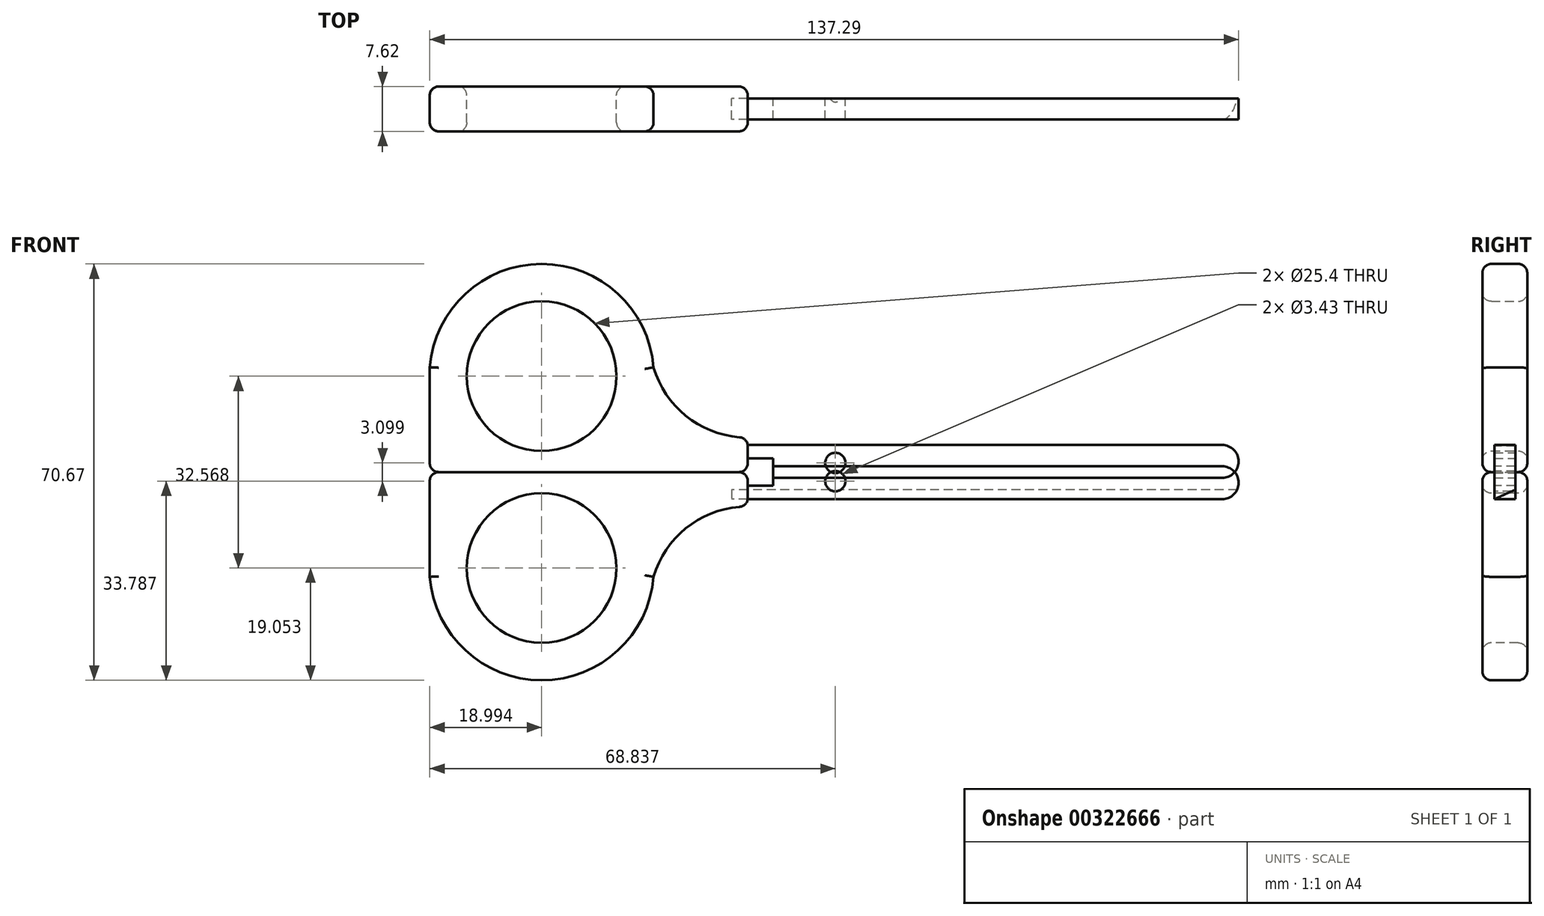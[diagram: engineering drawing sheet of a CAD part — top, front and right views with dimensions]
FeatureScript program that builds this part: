
annotation { "Feature Type Name" : "Feature", "Feature Type Description" : "" }
export const myFeature = defineFeature(function(context is Context, id is Id, definition is map)
    precondition{}
    {
        {
            var Q0;
            Q0=qCreatedBy(makeId("Front.planeOp"),FACE);
            var sketch = newSketch(context, id + "F0", { "sketchPlane" : qUnion([Q0])});
            skArc(sketch, "E0", {"start": v(-13.22, 18.69) * mm, "mid": v(-32.22, 36.24) * mm, "end": v(-51.2, 18.69) * mm});
            skLineSegment(sketch, "E1", {"start": v(-51.2, 18.69) * mm, "end": v(-51.2, 0.9) * mm});
            skLineSegment(sketch, "E2", {"start": v(-51.2, 0.9) * mm, "end": v(2.77, 0.9) * mm});
            skLineSegment(sketch, "E3", {"start": v(2.77, 0.9) * mm, "end": v(2.77, 6.77) * mm});
            skCircle(sketch, "E4", {"center": v(-32.22, 17.2) * mm, "radius": 12.7 * mm});
            skLineSegment(sketch, "E5", {"start": v(6.8, 7.3) * mm, "end": v(6.8, 7.3) * mm});
            skArc(sketch, "E6.filletArc", {"start": v(-13.22, 18.69) * mm, "mid": v(-5.52, 8.93) * mm, "end": v(6.8, 7.3) * mm});
            skSolve(sketch);
        }
        {
            var Q0;
            Q0=qSketchRegion(id+"F0",true);
            extrude(context, id + "F1", {"entities" : qUnion([Q0]), "endBound" : BoundingType.SYMMETRIC, "depth" : 7.62 * mm});
        }
        {
            var Q0;
            Q0=makeQuery(id+"F1.opExtrude","CAP_EDGE",EDGE,{"disambiguationData":[OSD([sQuery(id+"F0.wireOp",EDGE,"9kog8hWk-n0xC-SFov-Do0S-5giGeTCsTdrN")])],"isStart":false});
            var Q1;
            Q1=makeQuery(id+"F1.opExtrude","CAP_EDGE",EDGE,{"disambiguationData":[OSD([sQuery(id+"F0.wireOp",EDGE,"9kog8hWk-n0xC-SFov-Do0S-5giGeTCsTdrN")])],"isStart":true});
            var Q2;
            Q2=makeQuery(id+"F1.opExtrude","CAP_EDGE",EDGE,{"disambiguationData":[OSD([sQuery(id+"F0.wireOp",EDGE,"E3")])],"isStart":false});
            var Q3;
            Q3=makeQuery(id+"F1.opExtrude","CAP_EDGE",EDGE,{"disambiguationData":[OSD([sQuery(id+"F0.wireOp",EDGE,"E2")])],"isStart":false});
            var Q4;
            Q4=makeQuery(id+"F1.opExtrude","SWEPT_EDGE",EDGE,{"disambiguationData":[OSD([sQuery(id+"F0.wireOp",EDGE,"E2"),sQuery(id+"F0.wireOp",EDGE,"E3")])]});
            var Q5;
            Q5=makeQuery(id+"F1.opExtrude","CAP_EDGE",EDGE,{"disambiguationData":[OSD([sQuery(id+"F0.wireOp",EDGE,"E4")])],"isStart":false});
            var Q6;
            Q6=makeQuery(id+"F1.opExtrude","CAP_EDGE",EDGE,{"disambiguationData":[OSD([sQuery(id+"F0.wireOp",EDGE,"E4")])],"isStart":true});
            var Q7;
            Q7=makeQuery(id+"F1.opExtrude","CAP_EDGE",EDGE,{"disambiguationData":[OSD([sQuery(id+"F0.wireOp",EDGE,"E1")])],"isStart":true});
            var Q8;
            Q8=makeQuery(id+"F1.opExtrude","CAP_EDGE",EDGE,{"disambiguationData":[OSD([sQuery(id+"F0.wireOp",EDGE,"E1")])],"isStart":false});
            var Q9;
            Q9=makeQuery(id+"F1.opExtrude","SWEPT_EDGE",EDGE,{"disambiguationData":[OSD([sQuery(id+"F0.wireOp",EDGE,"E1"),sQuery(id+"F0.wireOp",EDGE,"E2")])]});
            var Q10;
            Q10=makeQuery(id+"F1.opExtrude","CAP_EDGE",EDGE,{"disambiguationData":[OSD([sQuery(id+"F0.wireOp",EDGE,"E6.filletArc")])],"isStart":true});
            var Q11;
            Q11=makeQuery(id+"F1.opExtrude","CAP_EDGE",EDGE,{"disambiguationData":[OSD([sQuery(id+"F0.wireOp",EDGE,"E2")])],"isStart":true});
            var Q12;
            Q12=makeQuery(id+"F1.opExtrude","CAP_EDGE",EDGE,{"disambiguationData":[OSD([sQuery(id+"F0.wireOp",EDGE,"E3")])],"isStart":true});
            var Q13;
            Q13=makeQuery(id+"F1.opExtrude","CAP_EDGE",EDGE,{"disambiguationData":[OSD([sQuery(id+"F0.wireOp",EDGE,"E6.filletArc")])],"isStart":false});
            var Q14;
            Q14=makeQuery(id+"F1.opExtrude","CAP_EDGE",EDGE,{"disambiguationData":[OSD([sQuery(id+"F0.wireOp",EDGE,"E0")])],"isStart":false});
            var Q15;
            Q15=makeQuery(id+"F1.opExtrude","CAP_EDGE",EDGE,{"disambiguationData":[OSD([sQuery(id+"F0.wireOp",EDGE,"E0")])],"isStart":true});
            var Q16;
            Q16=makeQuery(id+"F1.opExtrude","SWEPT_EDGE",EDGE,{"disambiguationData":[OSD([sQuery(id+"F0.wireOp",EDGE,"E3"),sQuery(id+"F0.wireOp",EDGE,"E6.filletArc")])]});
            fillet(context, id + "F2", {"entities" : qUnion([Q0, Q1, Q2, Q3, Q4, Q5, Q6, Q7, Q8, Q9, Q10, Q11, Q12, Q13, Q14, Q15, Q16]), "radius" : 1.52 * mm, "tangentPropagation" : true, "allowEdgeOverflow" : false});
        }
        {
            var Q0;
            Q0=qCreatedBy(makeId("Front.planeOp"),FACE);
            var sketch = newSketch(context, id + "F3", { "sketchPlane" : qUnion([Q0])});
            skLineSegment(sketch, "E7", {"start": v(2.77, 5.5) * mm, "end": v(83.29, 5.5) * mm});
            skArc(sketch, "E8", {"start": v(83.29, -0.08) * mm, "mid": v(86.08, 2.71) * mm, "end": v(83.29, 5.5) * mm});
            skLineSegment(sketch, "E9", {"start": v(83.29, -0.08) * mm, "end": v(7.09, -0.08) * mm});
            skLineSegment(sketch, "E10", {"start": v(7.09, -0.08) * mm, "end": v(7.09, 3.22) * mm});
            skLineSegment(sketch, "E11", {"start": v(7.09, 3.22) * mm, "end": v(2.77, 3.22) * mm});
            skCircle(sketch, "E12", {"center": v(17.63, 2.46) * mm, "radius": 1.71 * mm});
            skLineSegment(sketch, "E13", {"start": v(2.77, 5.5) * mm, "end": v(2.77, 3.22) * mm});
            skSolve(sketch);
        }
        {
            var Q0;
            Q0=qSketchRegion(id+"F3",true);
            extrude(context, id + "F4", {"entities" : qUnion([Q0]), "operationType" : NewBodyOperationType.ADD, "endBound" : BoundingType.SYMMETRIC, "depth" : 3.56 * mm});
        }
        {
            var Q0;
            Q0=makeQuery(id+"F4.opExtrude","CAP_FACE",FACE,{"disambiguationData":[OSD([sQuery(id+"F3.wireOp",EDGE,"E7"),sQuery(id+"F3.wireOp",EDGE,"E8"),sQuery(id+"F3.wireOp",EDGE,"E9"),sQuery(id+"F3.wireOp",EDGE,"E10"),sQuery(id+"F3.wireOp",EDGE,"E11"),sQuery(id+"F3.wireOp",EDGE,"E12"),sQuery(id+"F3.wireOp",EDGE,"E13")])],"isStart":false});
            var sketch = newSketch(context, id + "F5", { "sketchPlane" : qUnion([Q0])});
            skLineSegment(sketch, "E14", {"start": v(92.67, -2.67) * mm, "end": v(92.67, 7.28) * mm});
            skLineSegment(sketch, "E15", {"start": v(92.67, 7.28) * mm, "end": v(83.29, 7.28) * mm});
            skLineSegment(sketch, "E16", {"start": v(83.29, 7.28) * mm, "end": v(83.29, 5.5) * mm});
            skArc(sketch, "E17", {"start": v(86.08, 2.71) * mm, "mid": v(85.26, 4.69) * mm, "end": v(83.29, 5.5) * mm});
            skLineSegment(sketch, "E18", {"start": v(86.08, 2.71) * mm, "end": v(86.08, -2.5) * mm});
            skLineSegment(sketch, "E19", {"start": v(86.08, -2.5) * mm, "end": v(92.67, -2.67) * mm});
            skSolve(sketch);
        }
        {
            var Q0;
            Q0=qSketchRegion(id+"F5",true);
            extrude(context, id + "F6", {"entities" : qUnion([Q0]), "operationType" : NewBodyOperationType.REMOVE, "endBound" : BoundingType.THROUGH_ALL, "oppositeDirection" : true, "depth" : 25.4 * mm});
        }
        {
            var Q0;
            Q0=makeQuery(id+"F1.opExtrude","SWEPT_BODY",BODY,{"disambiguationData":[OSD([sQuery(id+"F0.wireOp",EDGE,"E0"),sQuery(id+"F0.wireOp",EDGE,"E1"),sQuery(id+"F0.wireOp",EDGE,"E2"),sQuery(id+"F0.wireOp",EDGE,"E3"),sQuery(id+"F0.wireOp",EDGE,"E4"),sQuery(id+"F0.wireOp",EDGE,"E6.filletArc")])]});
            var Q1;
            Q1=sQuery(id+"F0.wireOp",EDGE,"E2");
            transform(context, id + "F7", {"entities" : qUnion([Q0]), "transformType" : TransformType.ROTATION, "transformAxis" : qUnion([Q1]), "angle" : 180 * degree, "makeCopy" : true});
        }
        {
            var Q0;
            Q0=qCreatedBy(makeId("Right.planeOp"),FACE);
            var sketch = newSketch(context, id + "F8", { "sketchPlane" : qUnion([Q0])});
            skLineSegment(sketch, "E20", {"start": v(-1.78, -3.7) * mm, "end": v(1.78, -2.08) * mm});
            skLineSegment(sketch, "E21", {"start": v(1.78, -2.08) * mm, "end": v(1.78, -3.7) * mm});
            skLineSegment(sketch, "E22", {"start": v(1.78, -3.7) * mm, "end": v(-1.78, -3.7) * mm});
            skSolve(sketch);
        }
        {
            var Q0;
            Q0 = qSketchRegion(id + "F8", true);
            extrude(context, id + "F9", {"entities" : qUnion([Q0]), "operationType" : NewBodyOperationType.REMOVE, "endBound" : BoundingType.THROUGH_ALL, "depth" : 25.4 * mm});
        }
    });
